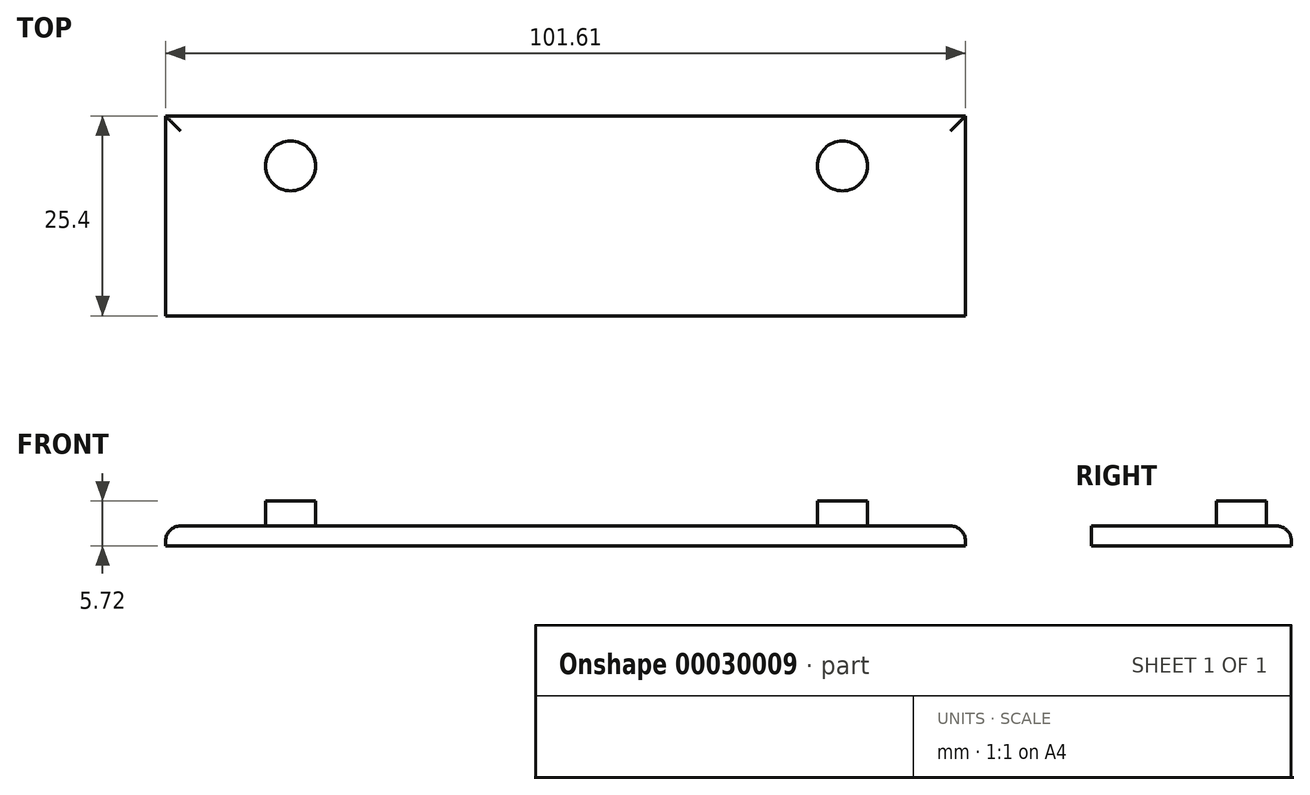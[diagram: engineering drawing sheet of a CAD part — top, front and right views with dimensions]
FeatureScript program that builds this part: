
annotation { "Feature Type Name" : "Feature", "Feature Type Description" : "" }
export const myFeature = defineFeature(function(context is Context, id is Id, definition is map)
    precondition{}
    {
        {
            var Q0;
            Q0=qCreatedBy(makeId("Top.planeOp"),FACE);
            var sketch = newSketch(context, id + "F0", { "sketchPlane" : qUnion([Q0])});
            skLineSegment(sketch, "E0.bottom", {"start": v(0, 0) * mm, "end": v(69.85, 0) * mm});
            skLineSegment(sketch, "E0.top", {"start": v(0, 6.35) * mm, "end": v(69.85, 6.35) * mm});
            skLineSegment(sketch, "E0.left", {"start": v(0, 0) * mm, "end": v(0, 6.35) * mm});
            skLineSegment(sketch, "E0.right", {"start": v(69.85, 0) * mm, "end": v(69.85, 6.35) * mm});
            skLineSegment(sketch, "E1.rect.bottom", {"start": v(85.73, -12.7) * mm, "end": v(-15.87, -12.7) * mm});
            skLineSegment(sketch, "E1.rect.top", {"start": v(85.73, 12.7) * mm, "end": v(-15.88, 12.7) * mm});
            skLineSegment(sketch, "E1.rect.left", {"start": v(85.73, -12.7) * mm, "end": v(85.73, 12.7) * mm});
            skLineSegment(sketch, "E1.rect.right", {"start": v(-15.87, -12.7) * mm, "end": v(-15.88, 12.7) * mm});
            skPoint(sketch, "E1.rect.middle", {"position": v(34.93, 0) * mm});
            skCircle(sketch, "E2", {"center": v(0, 6.35) * mm, "radius": 3.18 * mm});
            skCircle(sketch, "E3", {"center": v(69.85, 6.35) * mm, "radius": 3.18 * mm});
            skSolve(sketch);
        }
        {
            var Q0;
            {var subQ1=sQuery(id+"F0.wireOp",EDGE,"E0.top");var subQ4=sQuery(id+"F0.wireOp",EDGE,"E0.right");var subQ6=makeQuery(id+"F0.imprint","INTERSECT",VERTEX,{"derivedFrom":[subQ1,subQ4]});Q0=makeQuery(id+"F0.imprint","IMPRINT",FACE,{"disambiguationData":[TD([[makeQuery(id+"F0.imprint","IMPRINT",EDGE,{"disambiguationData":[TD([[subQ6,1.0]])],"derivedFrom":subQ1}),1.0]])]});}
            var Q1;
            {var subQ9=sQuery(id+"F0.wireOp",EDGE,"E0.bottom");Q1=makeQuery(id+"F0.imprint","IMPRINT",FACE,{"disambiguationData":[TD([[makeQuery(id+"F0.imprint","IMPRINT",EDGE,{"derivedFrom":subQ9}),1.0]])]});}
            var Q2;
            {var subQ11=sQuery(id+"F0.wireOp",EDGE,"E0.bottom");Q2=makeQuery(id+"F0.imprint","IMPRINT",FACE,{"disambiguationData":[TD([[makeQuery(id+"F0.imprint","IMPRINT",EDGE,{"derivedFrom":subQ11}),-1.0]])]});}
            var Q3;
            {var subQ0=sQuery(id+"F0.wireOp",EDGE,"E2");var subQ1=sQuery(id+"F0.wireOp",EDGE,"E0.top");var subQ2=makeQuery(id+"F0.imprint","INTERSECT",VERTEX,{"derivedFrom":[subQ1,subQ0]});Q3=makeQuery(id+"F0.imprint","IMPRINT",FACE,{"disambiguationData":[TD([[makeQuery(id+"F0.imprint","IMPRINT",EDGE,{"disambiguationData":[TD([[subQ2,-1.0]])],"derivedFrom":subQ1}),1.0]])]});}
            var Q4;
            {var subQ1=sQuery(id+"F0.wireOp",EDGE,"E0.left");var subQ4=sQuery(id+"F0.wireOp",EDGE,"E0.top");var subQ6=makeQuery(id+"F0.imprint","INTERSECT",VERTEX,{"derivedFrom":[subQ4,subQ1]});Q4=makeQuery(id+"F0.imprint","IMPRINT",FACE,{"disambiguationData":[TD([[makeQuery(id+"F0.imprint","IMPRINT",EDGE,{"disambiguationData":[TD([[subQ6,-1.0]])],"derivedFrom":subQ4}),1.0]])]});}
            var Q5;
            {var subQ1=sQuery(id+"F0.wireOp",EDGE,"E0.left");var subQ3=sQuery(id+"F0.wireOp",EDGE,"E0.top");var subQ5=makeQuery(id+"F0.imprint","INTERSECT",VERTEX,{"derivedFrom":[subQ3,subQ1]});Q5=makeQuery(id+"F0.imprint","IMPRINT",FACE,{"disambiguationData":[TD([[makeQuery(id+"F0.imprint","IMPRINT",EDGE,{"disambiguationData":[TD([[subQ5,-1.0]])],"derivedFrom":subQ3}),-1.0]])]});}
            var Q6;
            {var subQ1=sQuery(id+"F0.wireOp",EDGE,"E0.right");var subQ3=sQuery(id+"F0.wireOp",EDGE,"E0.top");var subQ5=makeQuery(id+"F0.imprint","INTERSECT",VERTEX,{"derivedFrom":[subQ3,subQ1]});Q6=makeQuery(id+"F0.imprint","IMPRINT",FACE,{"disambiguationData":[TD([[makeQuery(id+"F0.imprint","IMPRINT",EDGE,{"disambiguationData":[TD([[subQ5,1.0]])],"derivedFrom":subQ3}),-1.0]])]});}
            extrude(context, id + "F1", {"entities" : qUnion([Q0, Q1, Q2, Q3, Q4, Q5, Q6]), "depth" : 2.54 * mm});
        }
        {
            var Q0;
            Q0=makeQuery(id+"F1.opExtrude","CAP_EDGE",EDGE,{"disambiguationData":[OSD([sQuery(id+"F0.wireOp",EDGE,"E1.rect.top")])],"isStart":false});
            var Q1;
            Q1=makeQuery(id+"F1.opExtrude","CAP_EDGE",EDGE,{"disambiguationData":[OSD([sQuery(id+"F0.wireOp",EDGE,"E1.rect.right")])],"isStart":false});
            var Q2;
            Q2=makeQuery(id+"F1.opExtrude","CAP_EDGE",EDGE,{"disambiguationData":[OSD([sQuery(id+"F0.wireOp",EDGE,"E1.rect.left")])],"isStart":false});
            fillet(context, id + "F2", {"entities" : qUnion([Q0, Q1, Q2]), "radius" : 1.9 * mm, "tangentPropagation" : true, "allowEdgeOverflow" : false});
        }
        {
            var Q0;
            Q0=makeQuery(id+"F1.opExtrude","CAP_FACE",FACE,{"disambiguationData":[OSD([sQuery(id+"F0.wireOp",EDGE,"E1.rect.bottom"),sQuery(id+"F0.wireOp",EDGE,"E1.rect.top"),sQuery(id+"F0.wireOp",EDGE,"E1.rect.left"),sQuery(id+"F0.wireOp",EDGE,"E1.rect.right")])],"isStart":false});
            var sketch = newSketch(context, id + "F3", { "sketchPlane" : qUnion([Q0])});
            skLineSegment(sketch, "E4.bottom", {"start": v(0, 0) * mm, "end": v(70.1, 0) * mm});
            skLineSegment(sketch, "E4.top", {"start": v(0, 6.35) * mm, "end": v(70.1, 6.35) * mm});
            skLineSegment(sketch, "E4.left", {"start": v(0, 0) * mm, "end": v(0, 6.35) * mm});
            skLineSegment(sketch, "E4.right", {"start": v(70.1, 0) * mm, "end": v(70.1, 6.35) * mm});
            skCircle(sketch, "E5", {"center": v(0, 6.35) * mm, "radius": 3.17 * mm});
            skCircle(sketch, "E6", {"center": v(70.1, 6.35) * mm, "radius": 3.17 * mm});
            skSolve(sketch);
        }
        {
            var Q0;
            {var subQ1=sQuery(id+"F3.wireOp",EDGE,"E4.right");var subQ3=sQuery(id+"F3.wireOp",EDGE,"E4.top");var subQ5=makeQuery(id+"F3.imprint","INTERSECT",VERTEX,{"derivedFrom":[subQ3,subQ1]});Q0=makeQuery(id+"F3.imprint","IMPRINT",FACE,{"disambiguationData":[TD([[makeQuery(id+"F3.imprint","IMPRINT",EDGE,{"disambiguationData":[TD([[subQ5,1.0]])],"derivedFrom":subQ3}),-1.0]])]});}
            var Q1;
            {var subQ1=sQuery(id+"F3.wireOp",EDGE,"E4.right");var subQ3=sQuery(id+"F3.wireOp",EDGE,"E4.top");var subQ5=makeQuery(id+"F3.imprint","INTERSECT",VERTEX,{"derivedFrom":[subQ3,subQ1]});Q1=makeQuery(id+"F3.imprint","IMPRINT",FACE,{"disambiguationData":[TD([[makeQuery(id+"F3.imprint","IMPRINT",EDGE,{"disambiguationData":[TD([[subQ5,1.0]])],"derivedFrom":subQ3}),1.0]])]});}
            var Q2;
            {var subQ1=sQuery(id+"F3.wireOp",EDGE,"E4.left");var subQ3=sQuery(id+"F3.wireOp",EDGE,"E4.top");var subQ5=makeQuery(id+"F3.imprint","INTERSECT",VERTEX,{"derivedFrom":[subQ3,subQ1]});Q2=makeQuery(id+"F3.imprint","IMPRINT",FACE,{"disambiguationData":[TD([[makeQuery(id+"F3.imprint","IMPRINT",EDGE,{"disambiguationData":[TD([[subQ5,-1.0]])],"derivedFrom":subQ3}),-1.0]])]});}
            var Q3;
            {var subQ1=sQuery(id+"F3.wireOp",EDGE,"E4.left");var subQ3=sQuery(id+"F3.wireOp",EDGE,"E4.top");var subQ5=makeQuery(id+"F3.imprint","INTERSECT",VERTEX,{"derivedFrom":[subQ3,subQ1]});Q3=makeQuery(id+"F3.imprint","IMPRINT",FACE,{"disambiguationData":[TD([[makeQuery(id+"F3.imprint","IMPRINT",EDGE,{"disambiguationData":[TD([[subQ5,-1.0]])],"derivedFrom":subQ3}),1.0]])]});}
            extrude(context, id + "F4", {"entities" : qUnion([Q0, Q1, Q2, Q3]), "operationType" : NewBodyOperationType.ADD, "depth" : 3.17 * mm});
        }
    });
